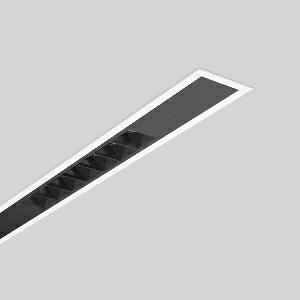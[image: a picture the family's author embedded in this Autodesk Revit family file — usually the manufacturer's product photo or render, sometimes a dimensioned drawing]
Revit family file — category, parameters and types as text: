
# Revit family: less_is_more_beamline_312475_002_1_1484
name_source: partatom
category: Lighting Fixtures
units: mm (PartAtom-declared; Revit-internal decimal feet)

## family parameters
Cut with Voids When Loaded = No
Host = Face
Light Source = No
Part Type = Normal
Room Calculation Point = No
Round Connector Dimension = Use Diameter
Shared = No

## types (1)
- LESS IS MORE BEAMLINE (1 x LED Modul 940, 1866.67 lm, 4000)
    Apparent Load = 72 VA
    CIE Flux Codes = 100 100 100 100 100
    Color Rendering = 92
    Color Temperature = 4000
    Default Elevation = 1800 mm
    Description = Series: LESS IS MORE BEAMLINE
Linear recessed ceiling and wall luminaire for aesthetically sophisticated lighting. Luminaire with three LED light units. Housing: extruded aluminium profile, powder-coated. End cap aluminium powder-coated. LED light unit with MRS technology: Mini-Reflector-System made of metallised thermoplastic with prismatic black glare-suppressing frame for pleasant glare-free light (RUG < 10). Each LED light unit has 7 reflector elements. Medium beam light distribution. Ceiling installation with pre-assembled SBS mounting system. LED unit with integrated converter interchangeable and removable. Suitable for through-wiring. 
Colour: traffic white, matt (RAL 9016)
Length: 1702 mm
Width: 71 mm
Height: 1.5 mm
Cut-out length: 1688 mm
Cut-out width: 60 mm
Recess height: 125 mm
Luminaire: recess height: 106 mm
Lamp: LED
Socket: without socket
Colour temperature: 4000K
Colour rendering index (CRI): 90
System power: 72 W
Rated luminous flux: 5600 lm
Luminous efficiency: 78 lm/W
Control gear: Regulated power supply
Protection class: I
Type of protection: IP 20
    Height = 0 mm  [stored 0 ft]
    Lamp = 1 x LED Modul 940
    Lamp Light Flux = 1866.67 lm
    Lamp count = 1
    Length = 1702 mm
    Lifetime = 50000 h
    Luminous efficacy = 78 lm/W
    Manufacturer = RZB
    ModVariant = No
    Model = 312475.002.1
    Mounting Place = Ceiling, Wall
    Mounting Type = Recessed
    Number of Poles = 1
    OnlyDefault = Yes
    Power Factor = 1
    Product Name = LESS IS MORE BEAMLINE
    Product group = Recessed LED linear luminaires
    ProductGroupID = 407
    Protection Class = Protection class I
    Protection Degree = IP 20
    RLX_Detail_Level = 1
    RLX_Emergency_Light_Flux = 0 lm
    RLX_Emergency_Type = 0
    RLX_Emergency_Type_DB = No
    RlxData = <blob elided: 23957 chars, md5=e8e4b11c>
    Socket = socket
    Standby Power = 0 W
    System Light Flux = 5600 lm
    System Power = 72 W
    Type Comments = Product without accessories
    Type Image = 312465.002.jpg
    URL = http://relux.com
    VarID = ---
    Voltage = 230 V
    Voltage Range = 220-240 V
    Weight = 0.00 kg
    Width = 71 mm

note: [stored X ft] marks values corroborated as IEEE doubles in the binary element streams (Revit-internal decimal feet)

## geometry (parser evidence)
native form markers: Blend x4, Sweep x18
no freeform markers — native parametric forms only
